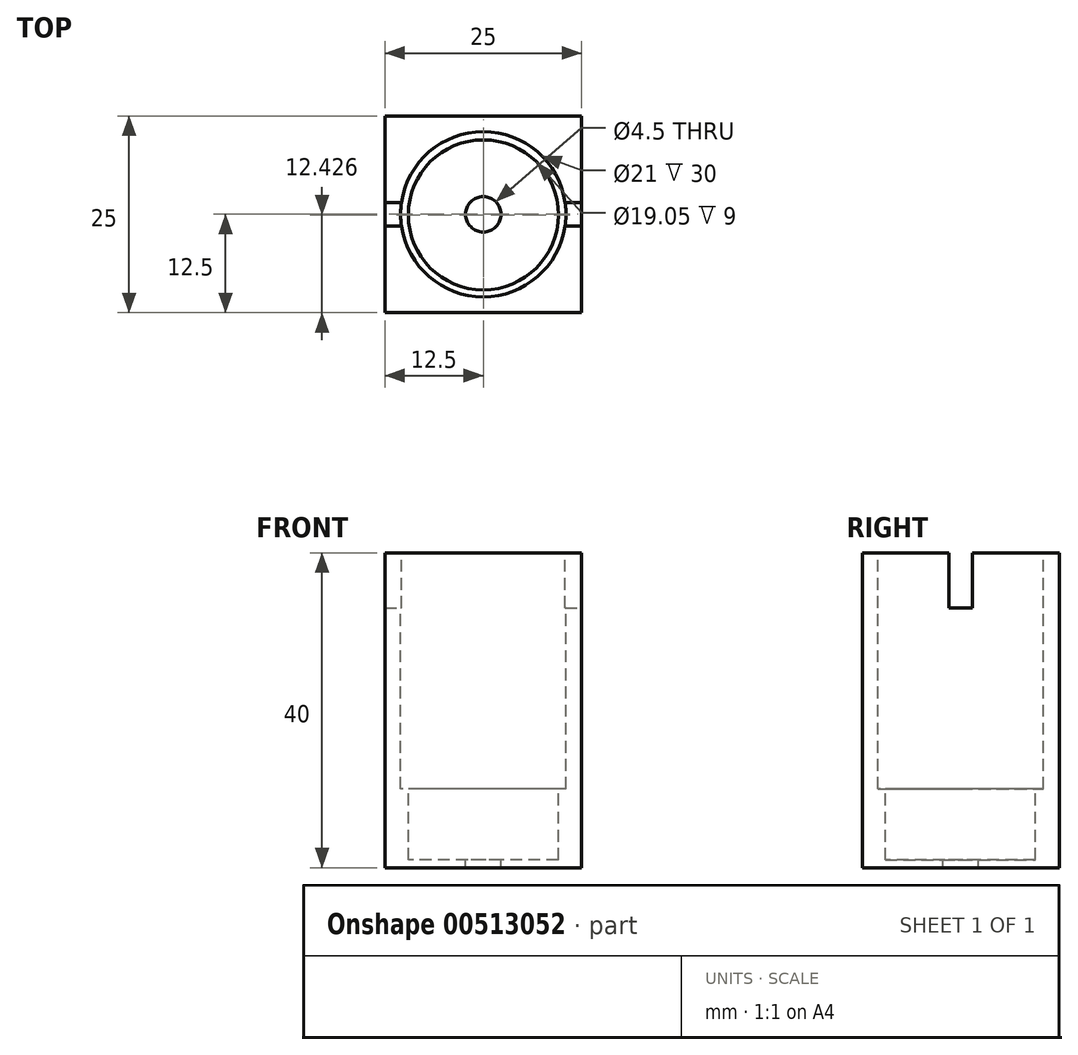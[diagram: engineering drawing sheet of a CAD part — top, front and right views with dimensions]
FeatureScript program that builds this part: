
annotation { "Feature Type Name" : "Feature", "Feature Type Description" : "" }
export const myFeature = defineFeature(function(context is Context, id is Id, definition is map)
    precondition{}
    {
        {
            var Q0;
            Q0=qCreatedBy(makeId("Top.planeOp"),FACE);
            var sketch = newSketch(context, id + "F0", { "sketchPlane" : qUnion([Q0])});
            skLineSegment(sketch, "E0.bottom", {"start": v(12.5, -12.5) * mm, "end": v(-12.5, -12.5) * mm});
            skLineSegment(sketch, "E0.top", {"start": v(12.5, 12.5) * mm, "end": v(-12.5, 12.5) * mm});
            skLineSegment(sketch, "E0.left", {"start": v(12.5, -12.5) * mm, "end": v(12.5, 12.5) * mm});
            skLineSegment(sketch, "E0.right", {"start": v(-12.5, -12.5) * mm, "end": v(-12.5, 12.5) * mm});
            skPoint(sketch, "E0.middle", {"position": v(0, 0) * mm});
            skSolve(sketch);
        }
        {
            var Q0;
            Q0=qSketchRegion(id+"F0",true);
            extrude(context, id + "F1", {"entities" : qUnion([Q0]), "depth" : 40 * mm});
        }
        {
            var Q0;
            Q0=makeQuery(id+"F1.opExtrude","CAP_FACE",FACE,{"disambiguationData":[OSD([sQuery(id+"F0.wireOp",EDGE,"E0.bottom"),sQuery(id+"F0.wireOp",EDGE,"E0.top"),sQuery(id+"F0.wireOp",EDGE,"E0.left"),sQuery(id+"F0.wireOp",EDGE,"E0.right")])],"isStart":false});
            var sketch = newSketch(context, id + "F2", { "sketchPlane" : qUnion([Q0])});
            skCircle(sketch, "E1", {"center": v(0, 0) * mm, "radius": 10.5 * mm});
            skSolve(sketch);
        }
        {
            var Q0;
            Q0=qSketchRegion(id+"F2",true);
            extrude(context, id + "F3", {"entities" : qUnion([Q0]), "operationType" : NewBodyOperationType.REMOVE, "oppositeDirection" : true, "depth" : 30 * mm, "offsetDistance" : 25 * mm});
        }
        {
            var Q0;
            Q0=makeQuery(id+"F3.boolean.opBoolean","COPY",FACE,{"derivedFrom":makeQuery(id+"F3.opExtrude","CAP_FACE",FACE,{"disambiguationData":[OSD([sQuery(id+"F2.wireOp",EDGE,"E1")])],"isStart":false})});
            var sketch = newSketch(context, id + "F4", { "sketchPlane" : qUnion([Q0])});
            skCircle(sketch, "E2", {"center": v(0, 0) * mm, "radius": 2.25 * mm});
            skSolve(sketch);
        }
        {
            var Q0;
            Q0 = qSketchRegion(id + "F4", true);
            extrude(context, id + "F5", {"entities" : qUnion([Q0]), "operationType" : NewBodyOperationType.REMOVE, "oppositeDirection" : true, "depth" : 25 * mm});
        }
        {
            var Q0;
            Q0=makeQuery(id+"F1.opExtrude","SWEPT_FACE",FACE,{"disambiguationData":[OSD([sQuery(id+"F0.wireOp",EDGE,"E0.left")])]});
            var sketch = newSketch(context, id + "F6", { "sketchPlane" : qUnion([Q0])});
            skLineSegment(sketch, "E3.bottom", {"start": v(-1.5, 40) * mm, "end": v(1.5, 40) * mm});
            skLineSegment(sketch, "E3.top", {"start": v(-1.5, 33) * mm, "end": v(1.5, 33) * mm});
            skLineSegment(sketch, "E3.left", {"start": v(-1.5, 40) * mm, "end": v(-1.5, 33) * mm});
            skLineSegment(sketch, "E3.right", {"start": v(1.5, 40) * mm, "end": v(1.5, 33) * mm});
            skSolve(sketch);
        }
        {
            var Q0;
            Q0 = qSketchRegion(id + "F6", true);
            extrude(context, id + "F7", {"entities" : qUnion([Q0]), "operationType" : NewBodyOperationType.REMOVE, "oppositeDirection" : true, "depth" : 25 * mm});
        }
        {
            var Q0;
            Q0=makeQuery(id+"F3.boolean.opBoolean","COPY",FACE,{"derivedFrom":makeQuery(id+"F3.opExtrude","CAP_FACE",FACE,{"disambiguationData":[OSD([sQuery(id+"F2.wireOp",EDGE,"E1")])],"isStart":false})});
            var sketch = newSketch(context, id + "F8", { "sketchPlane" : qUnion([Q0])});
            skCircle(sketch, "E4", {"center": v(0, -0.07) * mm, "radius": 9.53 * mm});
            skSolve(sketch);
        }
        {
            var Q0;
            Q0 = qSketchRegion(id + "F8", true);
            extrude(context, id + "F9", {"entities" : qUnion([Q0]), "operationType" : NewBodyOperationType.REMOVE, "oppositeDirection" : true, "depth" : 9 * mm, "offsetDistance" : 25 * mm});
        }
    });
